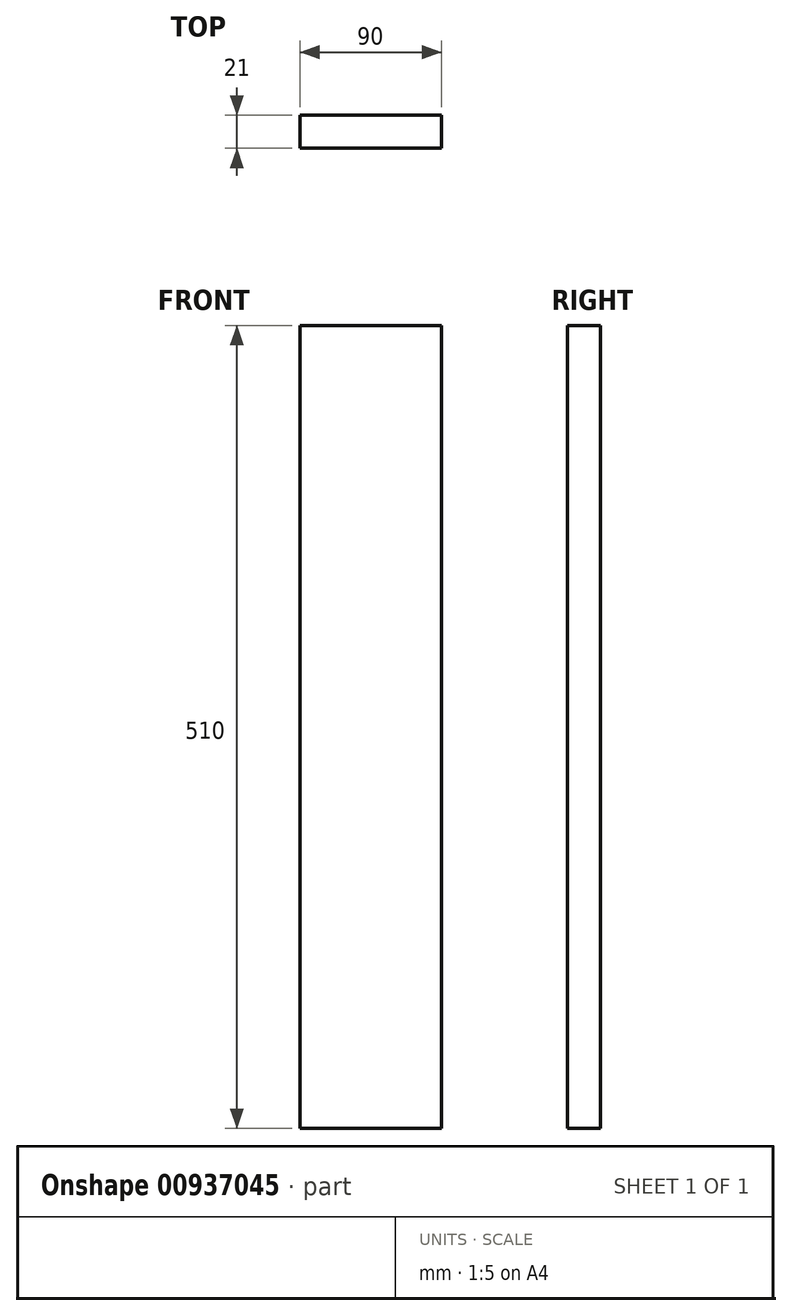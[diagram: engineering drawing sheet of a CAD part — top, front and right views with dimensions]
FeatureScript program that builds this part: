
annotation { "Feature Type Name" : "Feature", "Feature Type Description" : "" }
export const myFeature = defineFeature(function(context is Context, id is Id, definition is map)
    precondition{}
    {
        {
            var Q0;
            Q0=qCreatedBy(makeId("Top.planeOp"),FACE);
            var sketch = newSketch(context, id + "F0", { "sketchPlane" : qUnion([Q0])});
            skLineSegment(sketch, "E0.bottom", {"start": v(-45, -10.5) * mm, "end": v(45, -10.5) * mm});
            skLineSegment(sketch, "E0.top", {"start": v(-45, 10.5) * mm, "end": v(45, 10.5) * mm});
            skLineSegment(sketch, "E0.left", {"start": v(-45, -10.5) * mm, "end": v(-45, 10.5) * mm});
            skLineSegment(sketch, "E0.right", {"start": v(45, -10.5) * mm, "end": v(45, 10.5) * mm});
            skSolve(sketch);
        }
        {
            var Q0;
            Q0 = qSketchRegion(id + "F0", true);
            extrude(context, id + "F1", {"entities" : qUnion([Q0]), "depth" : 510 * mm, "offsetDistance" : 25 * mm});
        }
    });
